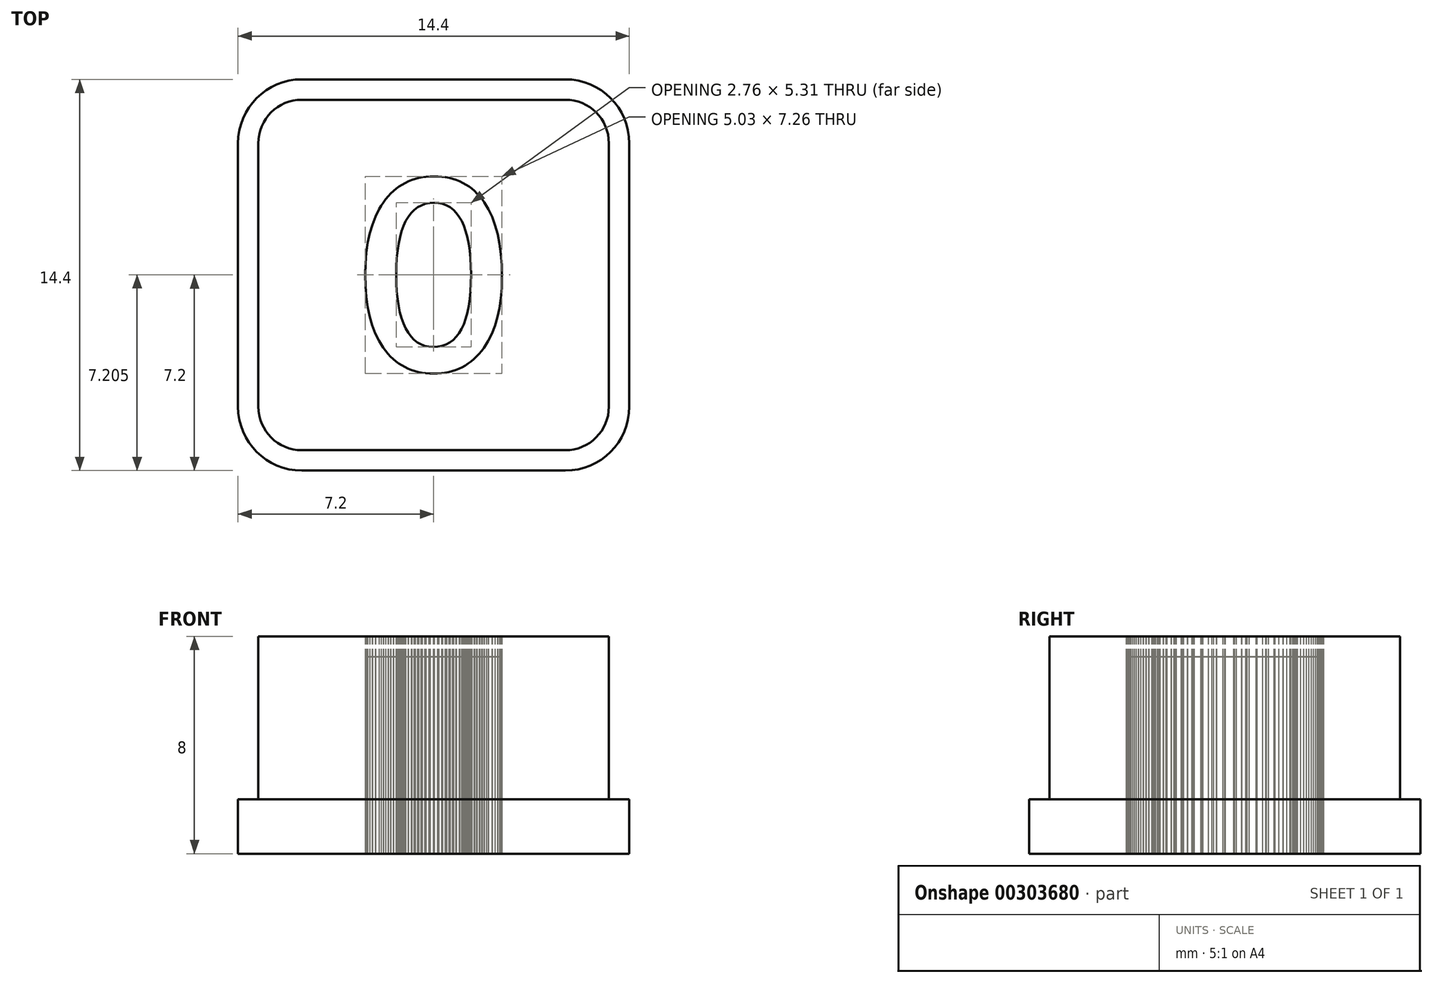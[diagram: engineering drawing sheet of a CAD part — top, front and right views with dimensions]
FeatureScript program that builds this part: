
annotation { "Feature Type Name" : "Feature", "Feature Type Description" : "" }
export const myFeature = defineFeature(function(context is Context, id is Id, definition is map)
    precondition{}
    {
        {
            var Q0;
            Q0=qCreatedBy(makeId("Top.planeOp"),FACE);
            var sketch = newSketch(context, id + "F0", { "sketchPlane" : qUnion([Q0])});
            skArc(sketch, "E0", {"start": v(4.85, -6.45) * mm, "mid": v(5.98, -5.98) * mm, "end": v(6.45, -4.85) * mm});
            skLineSegment(sketch, "E1", {"start": v(6.45, -4.85) * mm, "end": v(6.45, 4.85) * mm});
            skArc(sketch, "E2", {"start": v(6.45, 4.85) * mm, "mid": v(5.98, 5.98) * mm, "end": v(4.85, 6.45) * mm});
            skLineSegment(sketch, "E3", {"start": v(4.85, 6.45) * mm, "end": v(-4.85, 6.45) * mm});
            skArc(sketch, "E4", {"start": v(-4.85, 6.45) * mm, "mid": v(-5.98, 5.98) * mm, "end": v(-6.45, 4.85) * mm});
            skLineSegment(sketch, "E5", {"start": v(-6.45, 4.85) * mm, "end": v(-6.45, -4.85) * mm});
            skArc(sketch, "E6", {"start": v(-6.45, -4.85) * mm, "mid": v(-5.98, -5.98) * mm, "end": v(-4.85, -6.45) * mm});
            skLineSegment(sketch, "E7", {"start": v(-4.85, -6.45) * mm, "end": v(4.85, -6.45) * mm});
            skArc(sketch, "E8", {"start": v(-4.85, 7.2) * mm, "mid": v(-6.51, 6.51) * mm, "end": v(-7.2, 4.85) * mm});
            skLineSegment(sketch, "E9", {"start": v(-7.2, 4.85) * mm, "end": v(-7.2, -4.85) * mm});
            skArc(sketch, "E10", {"start": v(-7.2, -4.85) * mm, "mid": v(-6.51, -6.51) * mm, "end": v(-4.85, -7.2) * mm});
            skLineSegment(sketch, "E11", {"start": v(-4.85, -7.2) * mm, "end": v(4.85, -7.2) * mm});
            skArc(sketch, "E12", {"start": v(4.85, -7.2) * mm, "mid": v(6.51, -6.51) * mm, "end": v(7.2, -4.85) * mm});
            skLineSegment(sketch, "E13", {"start": v(7.2, -4.85) * mm, "end": v(7.2, 4.85) * mm});
            skArc(sketch, "E14", {"start": v(7.2, 4.85) * mm, "mid": v(6.51, 6.51) * mm, "end": v(4.85, 7.2) * mm});
            skLineSegment(sketch, "E15", {"start": v(4.85, 7.2) * mm, "end": v(-4.85, 7.2) * mm});
            skLineSegment(sketch, "E16", {"start": v(2.52, -0.07) * mm, "end": v(2.5, -0.48) * mm});
            skLineSegment(sketch, "E17", {"start": v(2.5, -0.48) * mm, "end": v(2.48, -0.86) * mm});
            skLineSegment(sketch, "E18", {"start": v(2.48, -0.86) * mm, "end": v(2.42, -1.22) * mm});
            skLineSegment(sketch, "E19", {"start": v(2.42, -1.22) * mm, "end": v(2.35, -1.56) * mm});
            skLineSegment(sketch, "E20", {"start": v(2.35, -1.56) * mm, "end": v(2.25, -1.87) * mm});
            skLineSegment(sketch, "E21", {"start": v(2.25, -1.87) * mm, "end": v(2.14, -2.17) * mm});
            skLineSegment(sketch, "E22", {"start": v(2.14, -2.17) * mm, "end": v(2, -2.44) * mm});
            skLineSegment(sketch, "E23", {"start": v(2, -2.44) * mm, "end": v(1.85, -2.68) * mm});
            skLineSegment(sketch, "E24", {"start": v(1.85, -2.68) * mm, "end": v(1.76, -2.8) * mm});
            skLineSegment(sketch, "E25", {"start": v(1.76, -2.8) * mm, "end": v(1.67, -2.9) * mm});
            skLineSegment(sketch, "E26", {"start": v(1.67, -2.9) * mm, "end": v(1.58, -3) * mm});
            skLineSegment(sketch, "E27", {"start": v(1.58, -3) * mm, "end": v(1.48, -3.1) * mm});
            skLineSegment(sketch, "E28", {"start": v(1.48, -3.1) * mm, "end": v(1.38, -3.18) * mm});
            skLineSegment(sketch, "E29", {"start": v(1.38, -3.18) * mm, "end": v(1.27, -3.26) * mm});
            skLineSegment(sketch, "E30", {"start": v(1.27, -3.26) * mm, "end": v(1.16, -3.33) * mm});
            skLineSegment(sketch, "E31", {"start": v(1.16, -3.33) * mm, "end": v(1.05, -3.4) * mm});
            skLineSegment(sketch, "E32", {"start": v(1.05, -3.4) * mm, "end": v(0.93, -3.45) * mm});
            skLineSegment(sketch, "E33", {"start": v(0.93, -3.45) * mm, "end": v(0.8, -3.5) * mm});
            skLineSegment(sketch, "E34", {"start": v(0.8, -3.5) * mm, "end": v(0.68, -3.54) * mm});
            skLineSegment(sketch, "E35", {"start": v(0.68, -3.54) * mm, "end": v(0.55, -3.57) * mm});
            skLineSegment(sketch, "E36", {"start": v(0.55, -3.57) * mm, "end": v(0.42, -3.6) * mm});
            skLineSegment(sketch, "E37", {"start": v(0.42, -3.6) * mm, "end": v(0.28, -3.61) * mm});
            skLineSegment(sketch, "E38", {"start": v(0.28, -3.61) * mm, "end": v(0.14, -3.63) * mm});
            skLineSegment(sketch, "E39", {"start": v(0.14, -3.63) * mm, "end": v(0, -3.63) * mm});
            skLineSegment(sketch, "E40", {"start": v(0, -3.63) * mm, "end": v(-0.15, -3.63) * mm});
            skLineSegment(sketch, "E41", {"start": v(-0.15, -3.63) * mm, "end": v(-0.3, -3.61) * mm});
            skLineSegment(sketch, "E42", {"start": v(-0.3, -3.61) * mm, "end": v(-0.43, -3.6) * mm});
            skLineSegment(sketch, "E43", {"start": v(-0.43, -3.6) * mm, "end": v(-0.56, -3.57) * mm});
            skLineSegment(sketch, "E44", {"start": v(-0.56, -3.57) * mm, "end": v(-0.7, -3.54) * mm});
            skLineSegment(sketch, "E45", {"start": v(-0.7, -3.54) * mm, "end": v(-0.82, -3.5) * mm});
            skLineSegment(sketch, "E46", {"start": v(-0.82, -3.5) * mm, "end": v(-0.94, -3.45) * mm});
            skLineSegment(sketch, "E47", {"start": v(-0.94, -3.45) * mm, "end": v(-1.06, -3.4) * mm});
            skLineSegment(sketch, "E48", {"start": v(-1.06, -3.4) * mm, "end": v(-1.17, -3.33) * mm});
            skLineSegment(sketch, "E49", {"start": v(-1.17, -3.33) * mm, "end": v(-1.28, -3.26) * mm});
            skLineSegment(sketch, "E50", {"start": v(-1.28, -3.26) * mm, "end": v(-1.39, -3.18) * mm});
            skLineSegment(sketch, "E51", {"start": v(-1.39, -3.18) * mm, "end": v(-1.5, -3.1) * mm});
            skLineSegment(sketch, "E52", {"start": v(-1.5, -3.1) * mm, "end": v(-1.59, -3) * mm});
            skLineSegment(sketch, "E53", {"start": v(-1.59, -3) * mm, "end": v(-1.68, -2.9) * mm});
            skLineSegment(sketch, "E54", {"start": v(-1.68, -2.9) * mm, "end": v(-1.77, -2.8) * mm});
            skLineSegment(sketch, "E55", {"start": v(-1.77, -2.8) * mm, "end": v(-1.86, -2.68) * mm});
            skLineSegment(sketch, "E56", {"start": v(-1.86, -2.68) * mm, "end": v(-1.94, -2.55) * mm});
            skLineSegment(sketch, "E57", {"start": v(-1.94, -2.55) * mm, "end": v(-2.01, -2.42) * mm});
            skLineSegment(sketch, "E58", {"start": v(-2.01, -2.42) * mm, "end": v(-2.14, -2.15) * mm});
            skLineSegment(sketch, "E59", {"start": v(-2.14, -2.15) * mm, "end": v(-2.26, -1.85) * mm});
            skLineSegment(sketch, "E60", {"start": v(-2.26, -1.85) * mm, "end": v(-2.35, -1.53) * mm});
            skLineSegment(sketch, "E61", {"start": v(-2.35, -1.53) * mm, "end": v(-2.42, -1.18) * mm});
            skLineSegment(sketch, "E62", {"start": v(-2.42, -1.18) * mm, "end": v(-2.48, -0.81) * mm});
            skLineSegment(sketch, "E63", {"start": v(-2.48, -0.81) * mm, "end": v(-2.5, -0.41) * mm});
            skLineSegment(sketch, "E64", {"start": v(-2.5, -0.41) * mm, "end": v(-2.52, 0) * mm});
            skLineSegment(sketch, "E65", {"start": v(-2.52, 0) * mm, "end": v(-2.5, 0.42) * mm});
            skLineSegment(sketch, "E66", {"start": v(-2.5, 0.42) * mm, "end": v(-2.48, 0.81) * mm});
            skLineSegment(sketch, "E67", {"start": v(-2.48, 0.81) * mm, "end": v(-2.42, 1.18) * mm});
            skLineSegment(sketch, "E68", {"start": v(-2.42, 1.18) * mm, "end": v(-2.35, 1.53) * mm});
            skLineSegment(sketch, "E69", {"start": v(-2.35, 1.53) * mm, "end": v(-2.26, 1.85) * mm});
            skLineSegment(sketch, "E70", {"start": v(-2.26, 1.85) * mm, "end": v(-2.14, 2.15) * mm});
            skLineSegment(sketch, "E71", {"start": v(-2.14, 2.15) * mm, "end": v(-2, 2.42) * mm});
            skLineSegment(sketch, "E72", {"start": v(-2, 2.42) * mm, "end": v(-1.93, 2.55) * mm});
            skLineSegment(sketch, "E73", {"start": v(-1.93, 2.55) * mm, "end": v(-1.85, 2.67) * mm});
            skLineSegment(sketch, "E74", {"start": v(-1.85, 2.67) * mm, "end": v(-1.76, 2.79) * mm});
            skLineSegment(sketch, "E75", {"start": v(-1.76, 2.79) * mm, "end": v(-1.67, 2.9) * mm});
            skLineSegment(sketch, "E76", {"start": v(-1.67, 2.9) * mm, "end": v(-1.58, 3) * mm});
            skLineSegment(sketch, "E77", {"start": v(-1.58, 3) * mm, "end": v(-1.48, 3.1) * mm});
            skLineSegment(sketch, "E78", {"start": v(-1.48, 3.1) * mm, "end": v(-1.38, 3.18) * mm});
            skLineSegment(sketch, "E79", {"start": v(-1.38, 3.18) * mm, "end": v(-1.27, 3.26) * mm});
            skLineSegment(sketch, "E80", {"start": v(-1.27, 3.26) * mm, "end": v(-1.16, 3.33) * mm});
            skLineSegment(sketch, "E81", {"start": v(-1.16, 3.33) * mm, "end": v(-1.05, 3.4) * mm});
            skLineSegment(sketch, "E82", {"start": v(-1.05, 3.4) * mm, "end": v(-0.93, 3.45) * mm});
            skLineSegment(sketch, "E83", {"start": v(-0.93, 3.45) * mm, "end": v(-0.8, 3.5) * mm});
            skLineSegment(sketch, "E84", {"start": v(-0.8, 3.5) * mm, "end": v(-0.68, 3.54) * mm});
            skLineSegment(sketch, "E85", {"start": v(-0.68, 3.54) * mm, "end": v(-0.55, 3.57) * mm});
            skLineSegment(sketch, "E86", {"start": v(-0.55, 3.57) * mm, "end": v(-0.42, 3.6) * mm});
            skLineSegment(sketch, "E87", {"start": v(-0.42, 3.6) * mm, "end": v(-0.28, 3.61) * mm});
            skLineSegment(sketch, "E88", {"start": v(-0.28, 3.61) * mm, "end": v(-0.13, 3.63) * mm});
            skLineSegment(sketch, "E89", {"start": v(-0.13, 3.63) * mm, "end": v(0.01, 3.63) * mm});
            skLineSegment(sketch, "E90", {"start": v(0.01, 3.63) * mm, "end": v(0.16, 3.63) * mm});
            skLineSegment(sketch, "E91", {"start": v(0.16, 3.63) * mm, "end": v(0.3, 3.61) * mm});
            skLineSegment(sketch, "E92", {"start": v(0.3, 3.61) * mm, "end": v(0.44, 3.6) * mm});
            skLineSegment(sketch, "E93", {"start": v(0.44, 3.6) * mm, "end": v(0.58, 3.57) * mm});
            skLineSegment(sketch, "E94", {"start": v(0.58, 3.57) * mm, "end": v(0.71, 3.54) * mm});
            skLineSegment(sketch, "E95", {"start": v(0.71, 3.54) * mm, "end": v(0.84, 3.5) * mm});
            skLineSegment(sketch, "E96", {"start": v(0.84, 3.5) * mm, "end": v(0.96, 3.45) * mm});
            skLineSegment(sketch, "E97", {"start": v(0.96, 3.45) * mm, "end": v(1.08, 3.39) * mm});
            skLineSegment(sketch, "E98", {"start": v(1.08, 3.39) * mm, "end": v(1.2, 3.33) * mm});
            skLineSegment(sketch, "E99", {"start": v(1.2, 3.33) * mm, "end": v(1.3, 3.25) * mm});
            skLineSegment(sketch, "E100", {"start": v(1.3, 3.25) * mm, "end": v(1.4, 3.18) * mm});
            skLineSegment(sketch, "E101", {"start": v(1.4, 3.18) * mm, "end": v(1.5, 3.09) * mm});
            skLineSegment(sketch, "E102", {"start": v(1.5, 3.09) * mm, "end": v(1.6, 3) * mm});
            skLineSegment(sketch, "E103", {"start": v(1.6, 3) * mm, "end": v(1.7, 2.9) * mm});
            skLineSegment(sketch, "E104", {"start": v(1.7, 2.9) * mm, "end": v(1.78, 2.79) * mm});
            skLineSegment(sketch, "E105", {"start": v(1.78, 2.79) * mm, "end": v(1.87, 2.67) * mm});
            skLineSegment(sketch, "E106", {"start": v(1.87, 2.67) * mm, "end": v(1.95, 2.55) * mm});
            skLineSegment(sketch, "E107", {"start": v(1.95, 2.55) * mm, "end": v(2.02, 2.42) * mm});
            skLineSegment(sketch, "E108", {"start": v(2.02, 2.42) * mm, "end": v(2.15, 2.14) * mm});
            skLineSegment(sketch, "E109", {"start": v(2.15, 2.14) * mm, "end": v(2.26, 1.84) * mm});
            skLineSegment(sketch, "E110", {"start": v(2.26, 1.84) * mm, "end": v(2.35, 1.5) * mm});
            skLineSegment(sketch, "E111", {"start": v(2.35, 1.5) * mm, "end": v(2.43, 1.15) * mm});
            skLineSegment(sketch, "E112", {"start": v(2.43, 1.15) * mm, "end": v(2.48, 0.77) * mm});
            skLineSegment(sketch, "E113", {"start": v(2.48, 0.77) * mm, "end": v(2.5, 0.36) * mm});
            skLineSegment(sketch, "E114", {"start": v(2.5, 0.36) * mm, "end": v(2.52, -0.07) * mm});
            skLineSegment(sketch, "E115", {"start": v(-0.02, -2.65) * mm, "end": v(0.15, -2.64) * mm});
            skLineSegment(sketch, "E116", {"start": v(0.15, -2.64) * mm, "end": v(0.3, -2.6) * mm});
            skLineSegment(sketch, "E117", {"start": v(0.3, -2.6) * mm, "end": v(0.45, -2.56) * mm});
            skLineSegment(sketch, "E118", {"start": v(0.45, -2.56) * mm, "end": v(0.59, -2.48) * mm});
            skLineSegment(sketch, "E119", {"start": v(0.59, -2.48) * mm, "end": v(0.72, -2.39) * mm});
            skLineSegment(sketch, "E120", {"start": v(0.72, -2.39) * mm, "end": v(0.83, -2.27) * mm});
            skLineSegment(sketch, "E121", {"start": v(0.83, -2.27) * mm, "end": v(0.93, -2.14) * mm});
            skLineSegment(sketch, "E122", {"start": v(0.93, -2.14) * mm, "end": v(1.03, -1.98) * mm});
            skLineSegment(sketch, "E123", {"start": v(1.03, -1.98) * mm, "end": v(1.11, -1.8) * mm});
            skLineSegment(sketch, "E124", {"start": v(1.11, -1.8) * mm, "end": v(1.18, -1.6) * mm});
            skLineSegment(sketch, "E125", {"start": v(1.18, -1.6) * mm, "end": v(1.24, -1.39) * mm});
            skLineSegment(sketch, "E126", {"start": v(1.24, -1.39) * mm, "end": v(1.3, -1.15) * mm});
            skLineSegment(sketch, "E127", {"start": v(1.3, -1.15) * mm, "end": v(1.33, -0.89) * mm});
            skLineSegment(sketch, "E128", {"start": v(1.33, -0.89) * mm, "end": v(1.36, -0.6) * mm});
            skLineSegment(sketch, "E129", {"start": v(1.36, -0.6) * mm, "end": v(1.37, -0.3) * mm});
            skLineSegment(sketch, "E130", {"start": v(1.37, -0.3) * mm, "end": v(1.38, 0.01) * mm});
            skLineSegment(sketch, "E131", {"start": v(1.38, 0.01) * mm, "end": v(1.37, 0.33) * mm});
            skLineSegment(sketch, "E132", {"start": v(1.37, 0.33) * mm, "end": v(1.36, 0.62) * mm});
            skLineSegment(sketch, "E133", {"start": v(1.36, 0.62) * mm, "end": v(1.33, 0.9) * mm});
            skLineSegment(sketch, "E134", {"start": v(1.33, 0.9) * mm, "end": v(1.3, 1.15) * mm});
            skLineSegment(sketch, "E135", {"start": v(1.3, 1.15) * mm, "end": v(1.24, 1.39) * mm});
            skLineSegment(sketch, "E136", {"start": v(1.24, 1.39) * mm, "end": v(1.18, 1.6) * mm});
            skLineSegment(sketch, "E137", {"start": v(1.18, 1.6) * mm, "end": v(1.11, 1.8) * mm});
            skLineSegment(sketch, "E138", {"start": v(1.11, 1.8) * mm, "end": v(1.03, 1.98) * mm});
            skLineSegment(sketch, "E139", {"start": v(1.03, 1.98) * mm, "end": v(0.94, 2.14) * mm});
            skLineSegment(sketch, "E140", {"start": v(0.94, 2.14) * mm, "end": v(0.84, 2.28) * mm});
            skLineSegment(sketch, "E141", {"start": v(0.84, 2.28) * mm, "end": v(0.73, 2.4) * mm});
            skLineSegment(sketch, "E142", {"start": v(0.73, 2.4) * mm, "end": v(0.6, 2.49) * mm});
            skLineSegment(sketch, "E143", {"start": v(0.6, 2.49) * mm, "end": v(0.48, 2.56) * mm});
            skLineSegment(sketch, "E144", {"start": v(0.48, 2.56) * mm, "end": v(0.33, 2.62) * mm});
            skLineSegment(sketch, "E145", {"start": v(0.33, 2.62) * mm, "end": v(0.18, 2.65) * mm});
            skLineSegment(sketch, "E146", {"start": v(0.18, 2.65) * mm, "end": v(0.02, 2.66) * mm});
            skLineSegment(sketch, "E147", {"start": v(0.02, 2.66) * mm, "end": v(-0.15, 2.65) * mm});
            skLineSegment(sketch, "E148", {"start": v(-0.15, 2.65) * mm, "end": v(-0.3, 2.62) * mm});
            skLineSegment(sketch, "E149", {"start": v(-0.3, 2.62) * mm, "end": v(-0.45, 2.56) * mm});
            skLineSegment(sketch, "E150", {"start": v(-0.45, 2.56) * mm, "end": v(-0.59, 2.49) * mm});
            skLineSegment(sketch, "E151", {"start": v(-0.59, 2.49) * mm, "end": v(-0.71, 2.4) * mm});
            skLineSegment(sketch, "E152", {"start": v(-0.71, 2.4) * mm, "end": v(-0.83, 2.28) * mm});
            skLineSegment(sketch, "E153", {"start": v(-0.83, 2.28) * mm, "end": v(-0.93, 2.14) * mm});
            skLineSegment(sketch, "E154", {"start": v(-0.93, 2.14) * mm, "end": v(-1.03, 1.98) * mm});
            skLineSegment(sketch, "E155", {"start": v(-1.03, 1.98) * mm, "end": v(-1.1, 1.8) * mm});
            skLineSegment(sketch, "E156", {"start": v(-1.1, 1.8) * mm, "end": v(-1.18, 1.6) * mm});
            skLineSegment(sketch, "E157", {"start": v(-1.18, 1.6) * mm, "end": v(-1.24, 1.39) * mm});
            skLineSegment(sketch, "E158", {"start": v(-1.24, 1.39) * mm, "end": v(-1.3, 1.15) * mm});
            skLineSegment(sketch, "E159", {"start": v(-1.3, 1.15) * mm, "end": v(-1.33, 0.9) * mm});
            skLineSegment(sketch, "E160", {"start": v(-1.33, 0.9) * mm, "end": v(-1.36, 0.61) * mm});
            skLineSegment(sketch, "E161", {"start": v(-1.36, 0.61) * mm, "end": v(-1.37, 0.31) * mm});
            skLineSegment(sketch, "E162", {"start": v(-1.37, 0.31) * mm, "end": v(-1.38, 0) * mm});
            skLineSegment(sketch, "E163", {"start": v(-1.38, 0) * mm, "end": v(-1.37, -0.31) * mm});
            skLineSegment(sketch, "E164", {"start": v(-1.37, -0.31) * mm, "end": v(-1.36, -0.6) * mm});
            skLineSegment(sketch, "E165", {"start": v(-1.36, -0.6) * mm, "end": v(-1.33, -0.88) * mm});
            skLineSegment(sketch, "E166", {"start": v(-1.33, -0.88) * mm, "end": v(-1.3, -1.13) * mm});
            skLineSegment(sketch, "E167", {"start": v(-1.3, -1.13) * mm, "end": v(-1.24, -1.37) * mm});
            skLineSegment(sketch, "E168", {"start": v(-1.24, -1.37) * mm, "end": v(-1.18, -1.59) * mm});
            skLineSegment(sketch, "E169", {"start": v(-1.18, -1.59) * mm, "end": v(-1.11, -1.78) * mm});
            skLineSegment(sketch, "E170", {"start": v(-1.11, -1.78) * mm, "end": v(-1.03, -1.97) * mm});
            skLineSegment(sketch, "E171", {"start": v(-1.03, -1.97) * mm, "end": v(-0.94, -2.13) * mm});
            skLineSegment(sketch, "E172", {"start": v(-0.94, -2.13) * mm, "end": v(-0.83, -2.26) * mm});
            skLineSegment(sketch, "E173", {"start": v(-0.83, -2.26) * mm, "end": v(-0.72, -2.38) * mm});
            skLineSegment(sketch, "E174", {"start": v(-0.72, -2.38) * mm, "end": v(-0.6, -2.48) * mm});
            skLineSegment(sketch, "E175", {"start": v(-0.6, -2.48) * mm, "end": v(-0.47, -2.55) * mm});
            skLineSegment(sketch, "E176", {"start": v(-0.47, -2.55) * mm, "end": v(-0.33, -2.6) * mm});
            skLineSegment(sketch, "E177", {"start": v(-0.33, -2.6) * mm, "end": v(-0.18, -2.64) * mm});
            skLineSegment(sketch, "E178", {"start": v(-0.18, -2.64) * mm, "end": v(-0.02, -2.65) * mm});
            skSolve(sketch);
        }
        {
            var Q0;
            Q0=makeQuery(id+"F0.imprint","IMPRINT",FACE,{"disambiguationData":[TD([[makeQuery(id+"F0.imprint","IMPRINT",EDGE,{"derivedFrom":sQuery(id+"F0.wireOp",EDGE,"E0")}),-1.0]])]});
            extrude(context, id + "F1", {"entities" : qUnion([Q0]), "depth" : 2 * mm});
        }
        {
            var Q0;
            Q0=makeQuery(id+"F0.imprint","IMPRINT",FACE,{"disambiguationData":[TD([[makeQuery(id+"F0.imprint","IMPRINT",EDGE,{"derivedFrom":sQuery(id+"F0.wireOp",EDGE,"E0")}),1.0]])]});
            var Q1;
            Q1=makeQuery(id+"F0.imprint","IMPRINT",FACE,{"disambiguationData":[TD([[makeQuery(id+"F0.imprint","IMPRINT",EDGE,{"derivedFrom":sQuery(id+"F0.wireOp",EDGE,"E115")}),1.0]])]});
            extrude(context, id + "F2", {"entities" : qUnion([Q0, Q1]), "operationType" : NewBodyOperationType.ADD, "depth" : 8 * mm});
        }
        {
            var Q0;
            Q0=makeQuery(id+"F0.imprint","IMPRINT",FACE,{"disambiguationData":[TD([[makeQuery(id+"F0.imprint","IMPRINT",EDGE,{"derivedFrom":sQuery(id+"F0.wireOp",EDGE,"E16")}),-1.0]])]});
            extrude(context, id + "F3", {"entities" : qUnion([Q0]), "depth" : 7.25 * mm});
        }
    });
